# Revit family: Single Hung - RE Cabins_Test
name_source: partatom
category: Windows
revit_build: Autodesk Revit 2015 (Build: 20140323_1530(x64)
units: mm (PartAtom-declared; Revit-internal decimal feet)

## types (5) — shared parameters
Assembly Code = B2020100
Construction Type Id = GSP4R
Glass Pane Material = Glass
Heat Transfer Coefficient (U) = 0.6496 BTU/(h·ft²·°F)
Sash Material = Sash
Solar Heat Gain Coefficient = 0.78
Thermal Resistance (R) = 1.5394 (h·ft²·°F)/BTU
Trim Exterior Material = Trim
Trim Interior Material = Trim
Trim Projection - Ext. = 0' - 0 1/2"
Trim Projection - Int. = 0' - 0 3/4"
Trim Width - Exterior = 0' - 3 1/2"
Trim Width - Interior = 0' - 3 1/2"
Visual Light Transmittance = 0.9
Wall Closure = By host
Window Inset = 0' - 0 3/4"

## per-type parameters (varying)
| type | Default Sill Height | Height | Width |
| 36" x 48" | 2' - 0" | 4' - 0" | 3' - 0" |
| 36" x 60" | 3' - 0" | 5' - 0" | 3' - 0" |
| 36" x 72" | 1' - 0" | 6' - 0" | 3' - 0" |
| 32" x 72" | 3' - 0" | 6' - 0" | 2' - 8 1/2" |
| 44" x 72" | 3' - 0" | 6' - 0" | 3' - 8 1/2" |

## geometry (parser evidence)
native form markers: Blend x8, Sweep x1
no freeform markers — native parametric forms only
